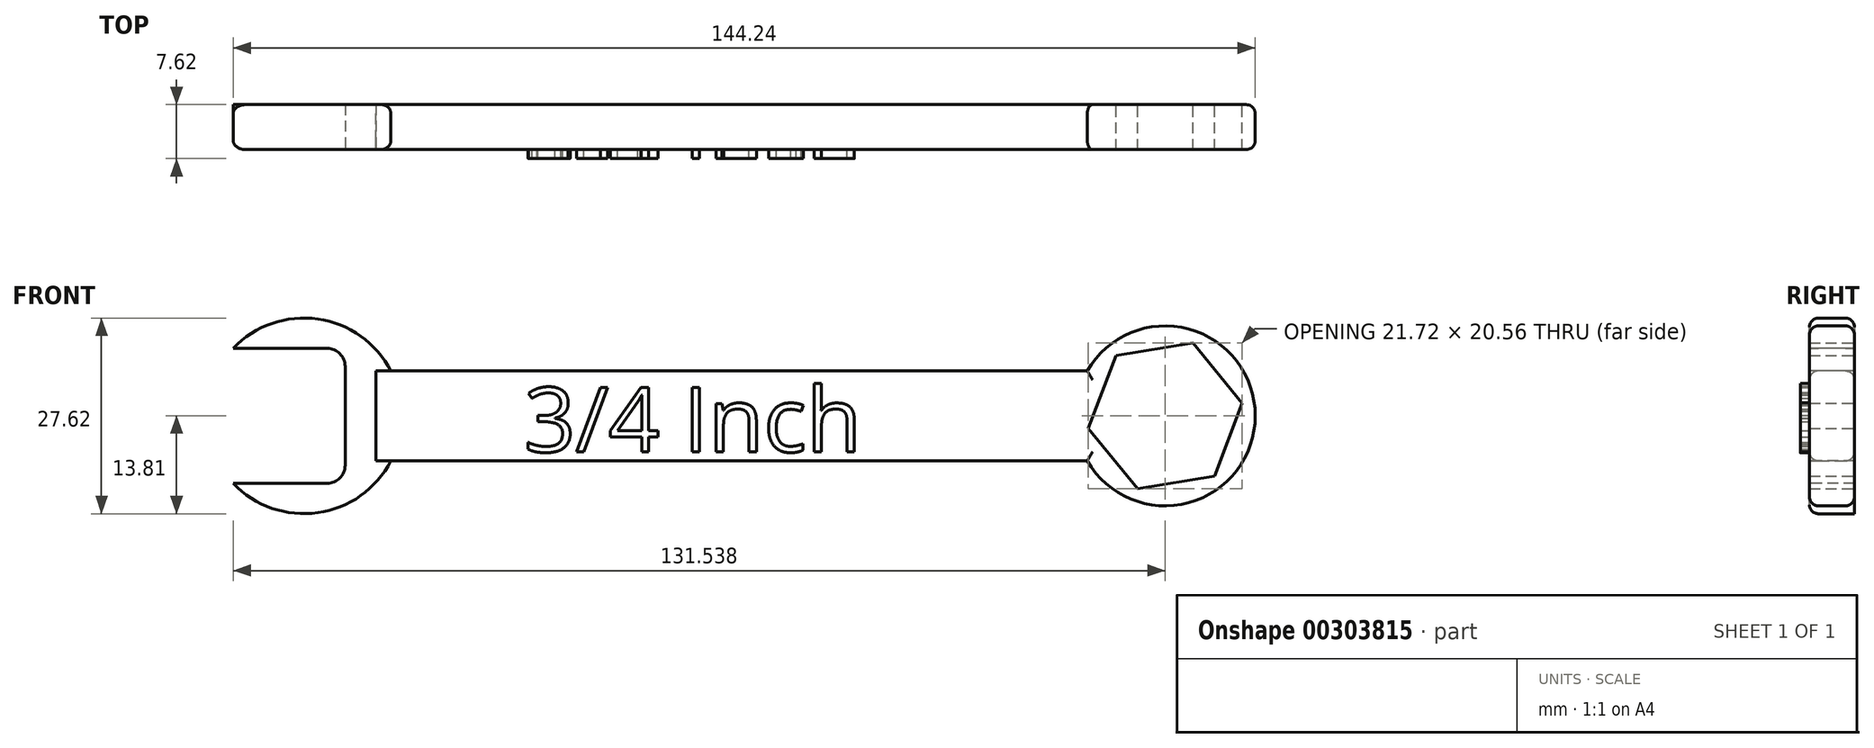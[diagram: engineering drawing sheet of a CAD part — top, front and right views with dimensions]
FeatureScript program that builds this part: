
annotation { "Feature Type Name" : "Feature", "Feature Type Description" : "" }
export const myFeature = defineFeature(function(context is Context, id is Id, definition is map)
    precondition{}
    {
        {
            var Q0;
            Q0=qCreatedBy(makeId("Front.planeOp"),FACE);
            var sketch = newSketch(context, id + "F0", { "sketchPlane" : qUnion([Q0])});
            skLineSegment(sketch, "E0.bottom", {"start": v(-50.19, 6.35) * mm, "end": v(51.41, 6.35) * mm});
            skLineSegment(sketch, "E0.top", {"start": v(-50.19, -6.35) * mm, "end": v(51.92, -6.35) * mm});
            skLineSegment(sketch, "E0.left", {"start": v(-50.19, 6.35) * mm, "end": v(-50.19, -6.35) * mm});
            skArc(sketch, "E1", {"start": v(50.19, -6.35) * mm, "mid": v(73.89, 0) * mm, "end": v(50.19, 6.35) * mm});
            skPoint(sketch, "E1.centerSnap0", {"position": v(51.66, 0) * mm});
            skCircle(sketch, "E2.cCircle", {"center": v(61.19, 0) * mm, "radius": 9.53 * mm, "construction": true});
            skLineSegment(sketch, "E2.0", {"start": v(72.05, 1.75) * mm, "end": v(68.14, -8.53) * mm});
            skLineSegment(sketch, "E2.1", {"start": v(68.14, -8.53) * mm, "end": v(57.28, -10.28) * mm});
            skLineSegment(sketch, "E2.2", {"start": v(57.28, -10.28) * mm, "end": v(50.33, -1.75) * mm});
            skLineSegment(sketch, "E2.3", {"start": v(50.33, -1.75) * mm, "end": v(54.24, 8.53) * mm});
            skLineSegment(sketch, "E2.4", {"start": v(54.24, 8.53) * mm, "end": v(65.1, 10.28) * mm});
            skLineSegment(sketch, "E2.5", {"start": v(65.1, 10.28) * mm, "end": v(72.05, 1.75) * mm});
            skPoint(sketch, "E2.0.midPoint", {"position": v(70.1, -3.39) * mm});
            skLineSegment(sketch, "E3", {"start": v(0, 0) * mm, "end": v(0, 28.3) * mm});
            skArc(sketch, "E4.MirrorCS", {"start": v(-50.19, -6.35) * mm, "mid": v(-73.89, 0) * mm, "end": v(-50.19, 6.35) * mm});
            skCircle(sketch, "E5.MirrorC", {"center": v(-61.19, 0) * mm, "radius": 9.53 * mm, "construction": true});
            skLineSegment(sketch, "E6.MirrorCS", {"start": v(-57.28, -10.28) * mm, "end": v(-50.33, -1.75) * mm});
            skPoint(sketch, "E7.MirrorP", {"position": v(-51.66, 0) * mm});
            skLineSegment(sketch, "E8.0", {"start": v(58.87, 2.84) * mm, "end": v(62.5, 3.43) * mm});
            skLineSegment(sketch, "E8.1", {"start": v(64.8, 0.58) * mm, "end": v(63.5, -2.84) * mm});
            skLineSegment(sketch, "E8.2", {"start": v(63.5, -2.84) * mm, "end": v(59.88, -3.43) * mm});
            skLineSegment(sketch, "E8.3", {"start": v(62.5, 3.43) * mm, "end": v(64.8, 0.58) * mm});
            skLineSegment(sketch, "E8.4", {"start": v(59.88, -3.43) * mm, "end": v(57.57, -0.58) * mm});
            skLineSegment(sketch, "E8.5", {"start": v(57.57, -0.58) * mm, "end": v(58.87, 2.84) * mm});
            skLineSegment(sketch, "E9.MirrorCS", {"start": v(-54.24, 8.53) * mm, "end": v(-65.1, 10.28) * mm});
            skLineSegment(sketch, "E10.MirrorCS", {"start": v(-58.87, 2.84) * mm, "end": v(-62.5, 3.43) * mm});
            skLineSegment(sketch, "E11.MirrorCS", {"start": v(-63.5, -2.84) * mm, "end": v(-59.88, -3.43) * mm});
            skLineSegment(sketch, "E12.MirrorCS", {"start": v(-57.57, -0.58) * mm, "end": v(-58.87, 2.84) * mm});
            skLineSegment(sketch, "E13.MirrorCS", {"start": v(-62.5, 3.43) * mm, "end": v(-64.8, 0.58) * mm});
            skLineSegment(sketch, "E14.MirrorCS", {"start": v(-64.8, 0.58) * mm, "end": v(-63.5, -2.84) * mm});
            skLineSegment(sketch, "E15.MirrorCS", {"start": v(-59.88, -3.43) * mm, "end": v(-57.57, -0.58) * mm});
            skPoint(sketch, "E16.MirrorP", {"position": v(-70.1, -3.39) * mm});
            skLineSegment(sketch, "E17.MirrorCS", {"start": v(-50.33, -1.75) * mm, "end": v(-54.24, 8.53) * mm});
            skPoint(sketch, "E18.orphan", {"position": v(-65.1, 10.28) * mm});
            skSolve(sketch);
        }
        {
            var Q0;
            {var subQ1=sQuery(id+"F0.wireOp",EDGE,"E0.left");Q0=makeQuery(id+"F0.imprint","IMPRINT",FACE,{"disambiguationData":[TD([[makeQuery(id+"F0.imprint","IMPRINT",EDGE,{"derivedFrom":subQ1}),1.0]])]});}
            extrude(context, id + "F1", {"entities" : qUnion([Q0]), "depth" : 6.35 * mm});
        }
        {
            var Q0;
            Q0=makeQuery(id+"F1.opExtrude","CAP_FACE",FACE,{"disambiguationData":[OSD([sQuery(id+"F0.wireOp",EDGE,"E0.bottom"),sQuery(id+"F0.wireOp",EDGE,"E0.top"),sQuery(id+"F0.wireOp",EDGE,"E0.left"),sQuery(id+"F0.wireOp",EDGE,"E1"),sQuery(id+"F0.wireOp",EDGE,"E2.0"),sQuery(id+"F0.wireOp",EDGE,"E2.1"),sQuery(id+"F0.wireOp",EDGE,"E2.2"),sQuery(id+"F0.wireOp",EDGE,"E2.3"),sQuery(id+"F0.wireOp",EDGE,"E2.5"),sQuery(id+"F0.wireOp",EDGE,"E2.4")])],"isStart":false});
            var sketch = newSketch(context, id + "F2", { "sketchPlane" : qUnion([Q0])});
            skArc(sketch, "E19", {"start": v(-70.35, -9.52) * mm, "mid": v(-46.54, 0) * mm, "end": v(-70.35, 9.52) * mm});
            skPoint(sketch, "E19.centerSnap0", {"position": v(-50.19, 0) * mm});
            skLineSegment(sketch, "E20", {"start": v(-60.35, 0) * mm, "end": v(-74.16, 0) * mm});
            skLineSegment(sketch, "E21.0", {"start": v(-50.19, -9.52) * mm, "end": v(-50.35, -9.52) * mm});
            skLineSegment(sketch, "E22.0", {"start": v(-50.19, 9.53) * mm, "end": v(-50.35, 9.53) * mm});
            skLineSegment(sketch, "E23", {"start": v(-54.56, 9.53) * mm, "end": v(-54.56, -9.52) * mm});
            skLineSegment(sketch, "E24.trimOffspring", {"start": v(-54.56, 9.53) * mm, "end": v(-70.35, 9.52) * mm});
            skLineSegment(sketch, "E25.trimOffspring", {"start": v(-54.56, -9.52) * mm, "end": v(-70.35, -9.53) * mm});
            skSolve(sketch);
        }
        {
            var Q0;
            Q0=makeQuery(id+"F2.imprint","IMPRINT",FACE,{"disambiguationData":[TD([[makeQuery(id+"F2.imprint","IMPRINT",EDGE,{"derivedFrom":sQuery(id+"F2.wireOp",EDGE,"E23")}),1.0]])]});
            extrude(context, id + "F3", {"entities" : qUnion([Q0]), "oppositeDirection" : true, "depth" : 6.35 * mm});
        }
        {
            var Q0;
            Q0=makeQuery(id+"F1.opExtrude","CAP_EDGE",EDGE,{"disambiguationData":[OSD([sQuery(id+"F0.wireOp",EDGE,"E0.top")])],"isStart":false});
            var Q1;
            Q1=makeQuery(id+"F1.opExtrude","CAP_EDGE",EDGE,{"disambiguationData":[OSD([sQuery(id+"F0.wireOp",EDGE,"E0.bottom")])],"isStart":false});
            var Q2;
            {var subQ0=sQuery(id+"F2.wireOp",EDGE,"E19");var subQ1=makeQuery(id+"F2.imprint","IMPRINT",VERTEX,{"disambiguationData":[OD(0.0)],"derivedFrom":subQ0});Q2=makeQuery(id+"F3.opExtrude","CAP_EDGE",EDGE,{"disambiguationData":[OSD([subQ0]),TDD([makeQuery(id+"F2.imprint","IMPRINT",EDGE,{"disambiguationData":[TD([[subQ1,1.0]])],"derivedFrom":subQ0}),makeQuery(id+"F2.imprint","IMPRINT",EDGE,{"disambiguationData":[TD([[subQ1,-1.0]])],"derivedFrom":subQ0})])],"isStart":true});}
            var Q3;
            Q3=makeQuery(id+"F1.opExtrude","CAP_EDGE",EDGE,{"disambiguationData":[OSD([sQuery(id+"F0.wireOp",EDGE,"E1")])],"isStart":false});
            var Q4;
            {var subQ0=sQuery(id+"F2.wireOp",EDGE,"E19");var subQ1=makeQuery(id+"F2.imprint","IMPRINT",VERTEX,{"disambiguationData":[OD(1.0)],"derivedFrom":subQ0});Q4=makeQuery(id+"F3.opExtrude","CAP_EDGE",EDGE,{"disambiguationData":[OSD([subQ0]),TDD([makeQuery(id+"F2.imprint","IMPRINT",EDGE,{"disambiguationData":[TD([[subQ1,1.0]])],"derivedFrom":subQ0}),makeQuery(id+"F2.imprint","IMPRINT",EDGE,{"disambiguationData":[TD([[subQ1,-1.0]])],"derivedFrom":subQ0})])],"isStart":true});}
            var Q5;
            Q5=makeQuery(id+"F1.opExtrude","CAP_EDGE",EDGE,{"disambiguationData":[OSD([sQuery(id+"F0.wireOp",EDGE,"E0.top")])],"isStart":true});
            var Q6;
            Q6=makeQuery(id+"F1.opExtrude","CAP_EDGE",EDGE,{"disambiguationData":[OSD([sQuery(id+"F0.wireOp",EDGE,"E0.bottom")])],"isStart":true});
            var Q7;
            {var subQ0=sQuery(id+"F2.wireOp",EDGE,"E19");var subQ1=makeQuery(id+"F2.imprint","IMPRINT",VERTEX,{"disambiguationData":[OD(1.0)],"derivedFrom":subQ0});Q7=makeQuery(id+"F3.opExtrude","CAP_EDGE",EDGE,{"disambiguationData":[OSD([subQ0]),TDD([makeQuery(id+"F2.imprint","IMPRINT",EDGE,{"disambiguationData":[TD([[subQ1,1.0]])],"derivedFrom":subQ0}),makeQuery(id+"F2.imprint","IMPRINT",EDGE,{"disambiguationData":[TD([[subQ1,-1.0]])],"derivedFrom":subQ0})])],"isStart":false});}
            var Q8;
            Q8=makeQuery(id+"F1.opExtrude","CAP_EDGE",EDGE,{"disambiguationData":[OSD([sQuery(id+"F0.wireOp",EDGE,"E1")])],"isStart":true});
            fillet(context, id + "F4", {"entities" : qUnion([Q0, Q1, Q2, Q3, Q4, Q5, Q6, Q7, Q8]), "radius" : 1.27 * mm, "tangentPropagation" : true, "allowEdgeOverflow" : false});
        }
        {
            var Q0;
            Q0=makeQuery(id+"F3.opExtrude","SWEPT_EDGE",EDGE,{"disambiguationData":[OSD([sQuery(id+"F2.wireOp",EDGE,"E23"),sQuery(id+"F2.wireOp",EDGE,"E24.trimOffspring")])]});
            var Q1;
            Q1=makeQuery(id+"F3.opExtrude","SWEPT_EDGE",EDGE,{"disambiguationData":[OSD([sQuery(id+"F2.wireOp",EDGE,"E23"),sQuery(id+"F2.wireOp",EDGE,"E25.trimOffspring")])]});
            fillet(context, id + "F5", {"entities" : qUnion([Q0, Q1]), "radius" : 2.54 * mm, "tangentPropagation" : true, "allowEdgeOverflow" : false});
        }
        {
            var Q0;
            Q0=makeQuery(id+"F1.opExtrude","CAP_FACE",FACE,{"disambiguationData":[OSD([sQuery(id+"F0.wireOp",EDGE,"E0.bottom"),sQuery(id+"F0.wireOp",EDGE,"E0.top"),sQuery(id+"F0.wireOp",EDGE,"E0.left"),sQuery(id+"F0.wireOp",EDGE,"E1"),sQuery(id+"F0.wireOp",EDGE,"E2.0"),sQuery(id+"F0.wireOp",EDGE,"E2.1"),sQuery(id+"F0.wireOp",EDGE,"E2.2"),sQuery(id+"F0.wireOp",EDGE,"E2.3"),sQuery(id+"F0.wireOp",EDGE,"E2.5"),sQuery(id+"F0.wireOp",EDGE,"E2.4")])],"isStart":false});
            var sketch = newSketch(context, id + "F6", { "sketchPlane" : qUnion([Q0])});
            skText(sketch, "E26", { "text": "3/4 Inch\n", "fontName": "OpenSans-Regular.ttf"});
            const initialGuessF6  = {"E26": [-0.0293, -0.00508, 1, 0, 0.00914]};
            skSetInitialGuess(sketch, initialGuessF6);
            skSolve(sketch);
        }
        {
            var Q0;
            Q0 = qSketchRegion(id + "F6", true);
            extrude(context, id + "F7", {"entities" : qUnion([Q0]), "operationType" : NewBodyOperationType.ADD, "depth" : 1.27 * mm});
        }
    });
